# Revit family: Dallmeier_Picoline_en
name_source: partatom
category: Sicherheitsgeräte
units: mm (PartAtom-declared; Revit-internal decimal feet)

## family parameters
Basisbauteil = Fläche
Beim Laden mit Abzugskörper schneiden = Nein
Bemaßung runder Anschluss = Durchmesser verwenden
Beschriftungsausrichtung beibehalten = Nein
Gemeinsam genutzt = Nein
Raumberechnungspunkt = Nein
Teiletyp = Normal

## types (4) — shared parameters
4:3 Available = Ja
Hersteller = Dallmeier electronic GmbH
Pixel Horizontal 16:9 = 2592
Pixel Horizontal 4:3 = 2592
URL = https://www.dallmeier.com
Vorgabe-Ansicht = 122 cm
number of sensors = 1
power consumption = 6 W
voltage supply = 12 V

## per-type parameters (varying)
| type | Maximal Horizontal FOV | Minimal Horizontal FOV | Modell | Picoline_Box | Picoline_InCeiling | Picoline_Surface | dimensions | operating temperature | weight |
| Picoline DDF5050HDV In-Ceiling | 130,00° | 130,00° | Picoline DDF 5050 HDV In-Ceiling | Nein | Ja | Nein | Ø 95x63mm | −20°C to +40°C | 0,74 kg |
| Picoline DDF5050HDV Surface | 130,00° | 130,00° | Picoline DDF 5050 HDV Surface | Nein | Nein | Ja | Ø 93x66mm | −20°C to +40°C | 0,45 kg |
| Picoline DDF5050HD-DN Box 3-10mm | 111,00° | 31,90° | Picoline DDF 5050 HD-DN Box 3-10mm | Ja | Nein | Nein | 59x59x92mm | −20°C to +50°C | 0,30 kg |
| Picoline DDF5050HD-DN Box 12-40mm | 23,80° | 8,30° | Picoline DDF 5050 HD-DN Box 12-40mm | Ja | Nein | Nein | 59x59x92mm | −20°C to +50°C | 0,30 kg |

## geometry (parser evidence)
native form markers: Sweep x15
no freeform markers — native parametric forms only
